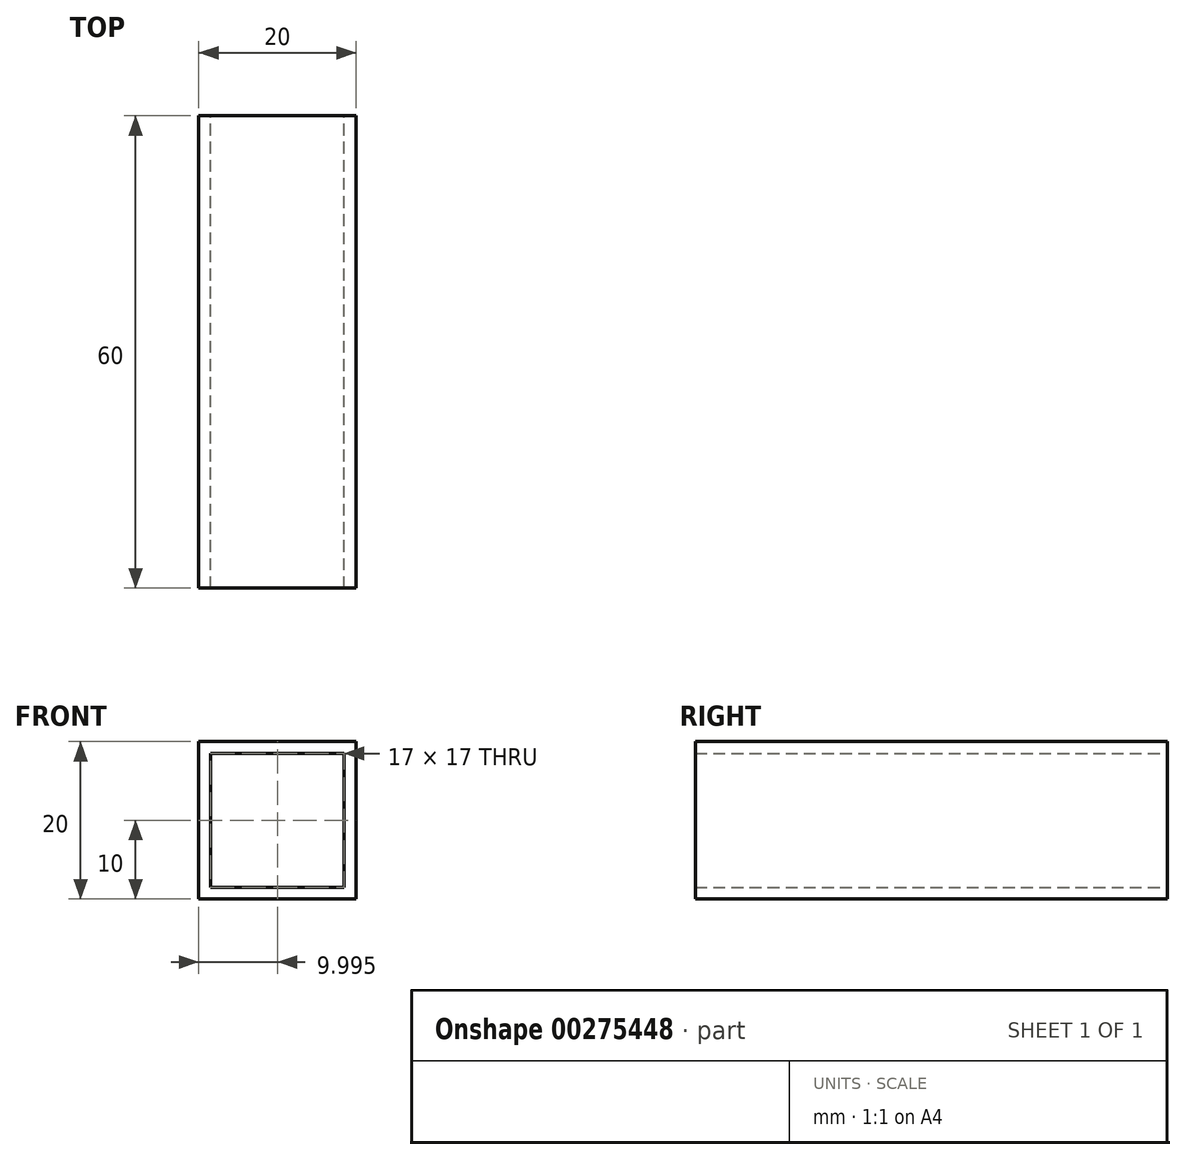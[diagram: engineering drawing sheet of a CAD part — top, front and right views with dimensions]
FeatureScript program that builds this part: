
annotation { "Feature Type Name" : "Feature", "Feature Type Description" : "" }
export const myFeature = defineFeature(function(context is Context, id is Id, definition is map)
    precondition{}
    {
        {
            var Q0;
            Q0=qCreatedBy(makeId("Front.planeOp"),FACE);
            var sketch = newSketch(context, id + "F0", { "sketchPlane" : qUnion([Q0])});
            skLineSegment(sketch, "E0.bottom", {"start": v(-34.48, 27.75) * mm, "end": v(-54.48, 27.75) * mm});
            skLineSegment(sketch, "E0.top", {"start": v(-34.48, 47.75) * mm, "end": v(-54.48, 47.75) * mm});
            skLineSegment(sketch, "E0.left", {"start": v(-34.48, 27.75) * mm, "end": v(-34.48, 47.75) * mm});
            skLineSegment(sketch, "E0.right", {"start": v(-54.48, 27.75) * mm, "end": v(-54.48, 47.75) * mm});
            skPoint(sketch, "E0.middle", {"position": v(-44.48, 37.75) * mm});
            skLineSegment(sketch, "E1.bottom", {"start": v(-35.98, 29.25) * mm, "end": v(-52.98, 29.25) * mm});
            skLineSegment(sketch, "E1.top", {"start": v(-35.98, 46.25) * mm, "end": v(-52.98, 46.25) * mm});
            skLineSegment(sketch, "E1.left", {"start": v(-35.98, 29.25) * mm, "end": v(-35.98, 46.25) * mm});
            skLineSegment(sketch, "E1.right", {"start": v(-52.98, 29.25) * mm, "end": v(-52.98, 46.25) * mm});
            skSolve(sketch);
        }
        {
            var Q0;
            Q0=makeQuery(id+"F0.imprint","IMPRINT",FACE,{"disambiguationData":[TD([[makeQuery(id+"F0.imprint","IMPRINT",EDGE,{"derivedFrom":sQuery(id+"F0.wireOp",EDGE,"E0.bottom")}),-1.0]])]});
            extrude(context, id + "F1", {"entities" : qUnion([Q0]), "depth" : 60 * mm});
        }
    });
